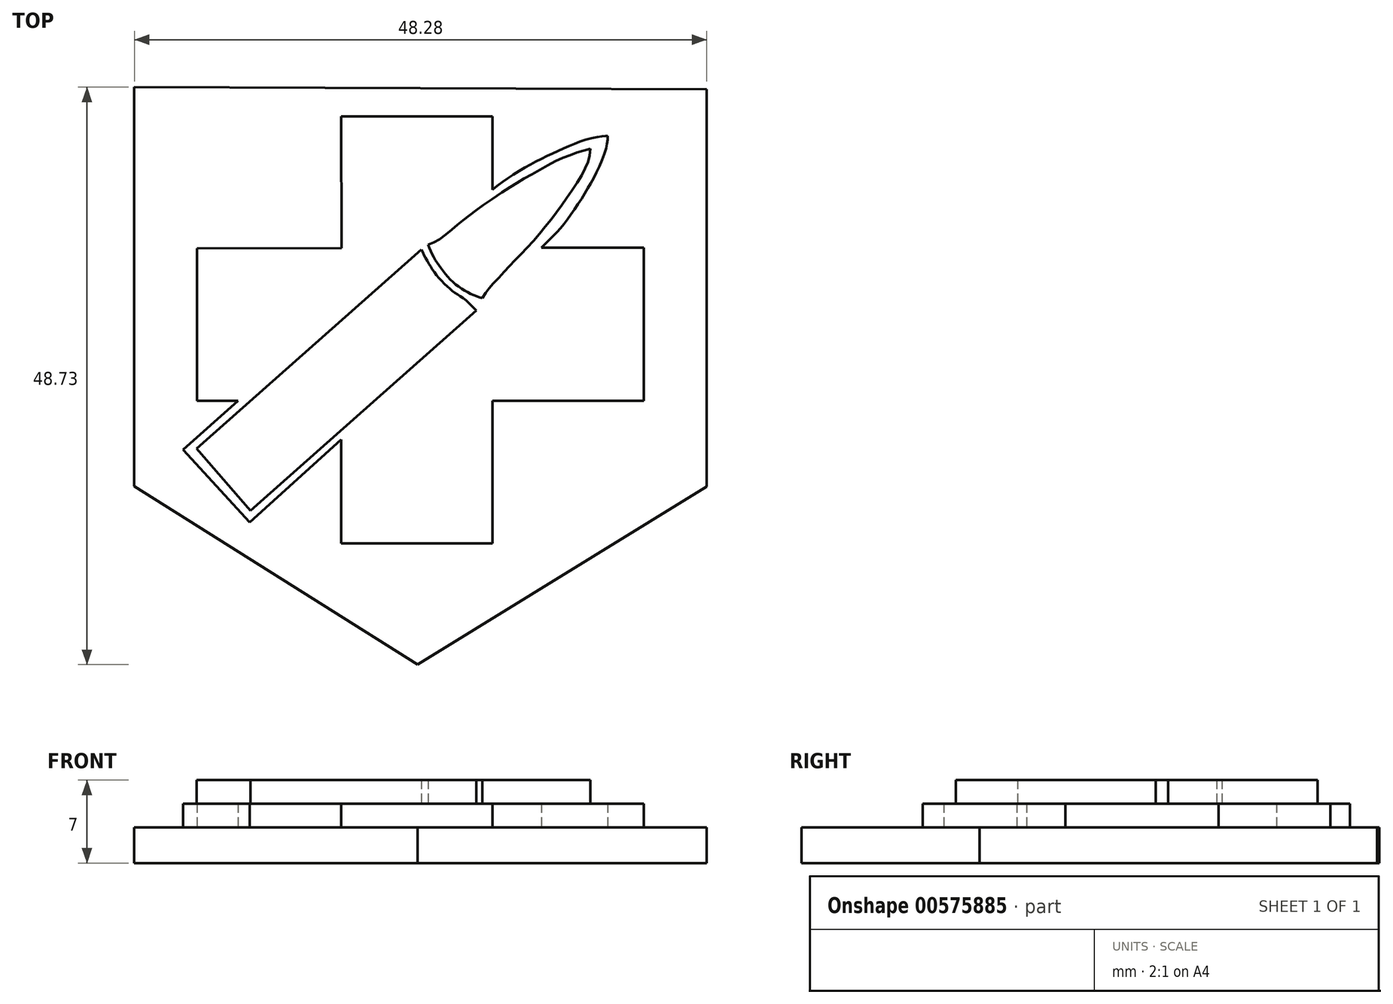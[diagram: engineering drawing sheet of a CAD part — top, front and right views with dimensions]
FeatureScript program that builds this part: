
annotation { "Feature Type Name" : "Feature", "Feature Type Description" : "" }
export const myFeature = defineFeature(function(context is Context, id is Id, definition is map)
    precondition{}
    {
        {
            var Q0;
            Q0=qCreatedBy(makeId("Top.planeOp"),FACE);
            var sketch = newSketch(context, id + "F0", { "sketchPlane" : qUnion([Q0])});
            skFitSpline(sketch, "E0", {"points": [v(11.07, 59.29) * mm, v(59.35, 59.1) * mm], "startDerivative": vector(48.28, -0.18) * mm, "endDerivative": vector(48.28, -0.18) * mm});
            skFitSpline(sketch, "E1", {"points": [v(59.35, 59.1) * mm, v(59.35, 25.58) * mm], "startDerivative": vector(0, -33.53) * mm, "endDerivative": vector(0, -33.53) * mm});
            skFitSpline(sketch, "E2", {"points": [v(11.07, 59.29) * mm, v(11.07, 25.61) * mm], "startDerivative": vector(0, -33.68) * mm, "endDerivative": vector(0, -33.68) * mm});
            skFitSpline(sketch, "E3", {"points": [v(11.07, 25.61) * mm, v(34.95, 10.56) * mm], "startDerivative": vector(23.88, -15.05) * mm, "endDerivative": vector(23.88, -15.05) * mm});
            skFitSpline(sketch, "E4", {"points": [v(34.95, 10.56) * mm, v(59.35, 25.58) * mm], "startDerivative": vector(24.4, 15.01) * mm, "endDerivative": vector(24.4, 15.01) * mm});
            skSolve(sketch);
        }
        {
            var Q0;
            Q0 = qSketchRegion(id + "F0", true);
            extrude(context, id + "F1", {"entities" : qUnion([Q0]), "depth" : 3 * mm, "offsetDistance" : 25 * mm});
        }
        {
            var Q0;
            Q0=makeQuery(id+"F1.opExtrude","CAP_FACE",FACE,{"disambiguationData":[OSD([sQuery(id+"F0.wireOp",EDGE,"E0"),sQuery(id+"F0.wireOp",EDGE,"E1"),sQuery(id+"F0.wireOp",EDGE,"E2"),sQuery(id+"F0.wireOp",EDGE,"E3"),sQuery(id+"F0.wireOp",EDGE,"E4")])],"isStart":false});
            var sketch = newSketch(context, id + "F2", { "sketchPlane" : qUnion([Q0])});
            skFitSpline(sketch, "E5", {"points": [v(28.55, 45.71) * mm, v(28.52, 56.81) * mm], "startDerivative": vector(-0.03, 11.1) * mm, "endDerivative": vector(-0.03, 11.1) * mm});
            skFitSpline(sketch, "E6", {"points": [v(28.52, 56.81) * mm, v(41.27, 56.81) * mm], "startDerivative": vector(12.74, 0) * mm, "endDerivative": vector(12.74, 0) * mm});
            skFitSpline(sketch, "E7", {"points": [v(41.27, 56.81) * mm, v(41.27, 50.62) * mm], "startDerivative": vector(0, -6.19) * mm, "endDerivative": vector(0, -6.19) * mm});
            skFitSpline(sketch, "E8", {"points": [v(41.27, 50.62) * mm, v(41.97, 51.19) * mm, v(43.8, 52.39) * mm, v(45.62, 53.35) * mm, v(47.4, 54.17) * mm, v(49.09, 54.84) * mm, v(50.6, 55.16) * mm, v(51, 55.18) * mm], "startDerivative": vector(5.35, 4.6) * mm, "endDerivative": vector(4.47, -0.09) * mm});
            skFitSpline(sketch, "E9", {"points": [v(51, 55.18) * mm, v(50.87, 54.17) * mm, v(50, 52) * mm, v(49, 50.2) * mm, v(47.74, 48.32) * mm, v(46.64, 46.97) * mm, v(45.4, 45.74) * mm], "startDerivative": vector(-0.36, -7.3) * mm, "endDerivative": vector(-7.9, -7.49) * mm});
            skFitSpline(sketch, "E10", {"points": [v(45.4, 45.74) * mm, v(54.03, 45.74) * mm], "startDerivative": vector(8.64, 0) * mm, "endDerivative": vector(8.64, 0) * mm});
            skFitSpline(sketch, "E11", {"points": [v(54.03, 45.74) * mm, v(54.03, 32.82) * mm], "startDerivative": vector(0, -12.93) * mm, "endDerivative": vector(0, -12.93) * mm});
            skFitSpline(sketch, "E12", {"points": [v(54.03, 32.82) * mm, v(41.27, 32.82) * mm], "startDerivative": vector(-12.76, 0) * mm, "endDerivative": vector(-12.76, 0) * mm});
            skFitSpline(sketch, "E13", {"points": [v(41.27, 32.82) * mm, v(41.27, 20.78) * mm], "startDerivative": vector(0, -12.04) * mm, "endDerivative": vector(0, -12.04) * mm});
            skFitSpline(sketch, "E14", {"points": [v(41.27, 20.78) * mm, v(28.52, 20.78) * mm], "startDerivative": vector(-12.74, 0) * mm, "endDerivative": vector(-12.74, 0) * mm});
            skFitSpline(sketch, "E15", {"points": [v(28.52, 20.78) * mm, v(28.52, 29.55) * mm], "startDerivative": vector(0, 8.77) * mm, "endDerivative": vector(0, 8.77) * mm});
            skFitSpline(sketch, "E16", {"points": [v(28.52, 29.55) * mm, v(20.8, 22.55) * mm], "startDerivative": vector(-7.73, -7) * mm, "endDerivative": vector(-7.73, -7) * mm});
            skFitSpline(sketch, "E17", {"points": [v(20.8, 22.55) * mm, v(15.17, 28.7) * mm], "startDerivative": vector(-5.63, 6.15) * mm, "endDerivative": vector(-5.63, 6.15) * mm});
            skFitSpline(sketch, "E18", {"points": [v(15.17, 28.7) * mm, v(19.82, 32.82) * mm], "startDerivative": vector(4.65, 4.11) * mm, "endDerivative": vector(4.65, 4.11) * mm});
            skFitSpline(sketch, "E19", {"points": [v(19.82, 32.82) * mm, v(16.35, 32.82) * mm], "startDerivative": vector(-3.47, 0) * mm, "endDerivative": vector(-3.47, 0) * mm});
            skFitSpline(sketch, "E20", {"points": [v(16.35, 32.82) * mm, v(16.35, 45.7) * mm], "startDerivative": vector(0, 12.87) * mm, "endDerivative": vector(0, 12.87) * mm});
            skFitSpline(sketch, "E21", {"points": [v(16.35, 45.7) * mm, v(28.55, 45.71) * mm], "startDerivative": vector(12.2, 0.02) * mm, "endDerivative": vector(12.2, 0.02) * mm});
            skSolve(sketch);
        }
        {
            var Q0;
            Q0 = qSketchRegion(id + "F2", true);
            extrude(context, id + "F3", {"entities" : qUnion([Q0]), "operationType" : NewBodyOperationType.ADD, "depth" : 2 * mm, "offsetDistance" : 25 * mm});
        }
        {
            var Q0;
            Q0=makeQuery(id+"F3.opExtrude","CAP_FACE",FACE,{"disambiguationData":[OSD([sQuery(id+"F2.wireOp",EDGE,"E5"),sQuery(id+"F2.wireOp",EDGE,"E6"),sQuery(id+"F2.wireOp",EDGE,"E7"),sQuery(id+"F2.wireOp",EDGE,"E8"),sQuery(id+"F2.wireOp",EDGE,"E9"),sQuery(id+"F2.wireOp",EDGE,"E10"),sQuery(id+"F2.wireOp",EDGE,"E11"),sQuery(id+"F2.wireOp",EDGE,"E12"),sQuery(id+"F2.wireOp",EDGE,"E13"),sQuery(id+"F2.wireOp",EDGE,"E14"),sQuery(id+"F2.wireOp",EDGE,"E15"),sQuery(id+"F2.wireOp",EDGE,"E16"),sQuery(id+"F2.wireOp",EDGE,"E17"),sQuery(id+"F2.wireOp",EDGE,"E18"),sQuery(id+"F2.wireOp",EDGE,"E19"),sQuery(id+"F2.wireOp",EDGE,"E20"),sQuery(id+"F2.wireOp",EDGE,"E21")])],"isStart":false});
            var sketch = newSketch(context, id + "F4", { "sketchPlane" : qUnion([Q0])});
            skFitSpline(sketch, "E22", {"points": [v(35.86, 46) * mm, v(36.4, 46.22) * mm, v(37.16, 46.7) * mm, v(37.99, 47.4) * mm, v(38.69, 47.96) * mm, v(39.56, 48.63) * mm, v(40.59, 49.39) * mm, v(42.41, 50.62) * mm, v(43.43, 51.27) * mm, v(44.58, 51.92) * mm, v(45.78, 52.61) * mm, v(46.93, 53.2) * mm, v(47.92, 53.58) * mm, v(48.68, 53.86) * mm, v(49.55, 54.08) * mm], "startDerivative": vector(10.16, 3.52) * mm, "endDerivative": vector(14.02, 3.2) * mm});
            skFitSpline(sketch, "E23", {"points": [v(49.55, 54.08) * mm, v(49.41, 53.23) * mm, v(49.1, 52.43) * mm, v(48.49, 51.33) * mm, v(47.58, 50) * mm, v(46.76, 48.81) * mm, v(45.8, 47.6) * mm, v(44.75, 46.33) * mm, v(43.73, 45.22) * mm, v(42.8, 44.28) * mm, v(42.04, 43.43) * mm, v(41.24, 42.6) * mm, v(40.84, 42.09) * mm, v(40.41, 41.48) * mm], "startDerivative": vector(-1.5, -13.27) * mm, "endDerivative": vector(-7.31, -10.36) * mm});
            skFitSpline(sketch, "E24", {"points": [v(40.41, 41.48) * mm, v(39.6, 41.78) * mm, v(38.6, 42.34) * mm, v(37.65, 43.13) * mm, v(36.86, 44.13) * mm, v(36.3, 44.96) * mm, v(35.86, 46) * mm], "startDerivative": vector(-5.41, 1.8) * mm, "endDerivative": vector(-2.39, 6.52) * mm});
            skFitSpline(sketch, "E25", {"points": [v(35.28, 45.58) * mm, v(35.63, 44.9) * mm, v(36.05, 44.15) * mm, v(36.59, 43.4) * mm, v(37.4, 42.53) * mm, v(38.08, 41.96) * mm, v(38.77, 41.5) * mm, v(39.9, 40.44) * mm], "startDerivative": vector(2.64, -5.3) * mm, "endDerivative": vector(6.94, -8.04) * mm});
            skFitSpline(sketch, "E26", {"points": [v(35.28, 45.58) * mm, v(16.33, 28.78) * mm], "startDerivative": vector(-18.95, -16.8) * mm, "endDerivative": vector(-18.95, -16.8) * mm});
            skFitSpline(sketch, "E27", {"points": [v(16.33, 28.78) * mm, v(20.88, 23.56) * mm], "startDerivative": vector(4.55, -5.21) * mm, "endDerivative": vector(4.55, -5.21) * mm});
            skFitSpline(sketch, "E28", {"points": [v(20.88, 23.56) * mm, v(39.9, 40.44) * mm], "startDerivative": vector(19.02, 16.88) * mm, "endDerivative": vector(19.02, 16.88) * mm});
            skSolve(sketch);
        }
        {
            var Q0;
            Q0 = qSketchRegion(id + "F4", true);
            extrude(context, id + "F5", {"entities" : qUnion([Q0]), "operationType" : NewBodyOperationType.ADD, "depth" : 2 * mm, "offsetDistance" : 25 * mm});
        }
    });
